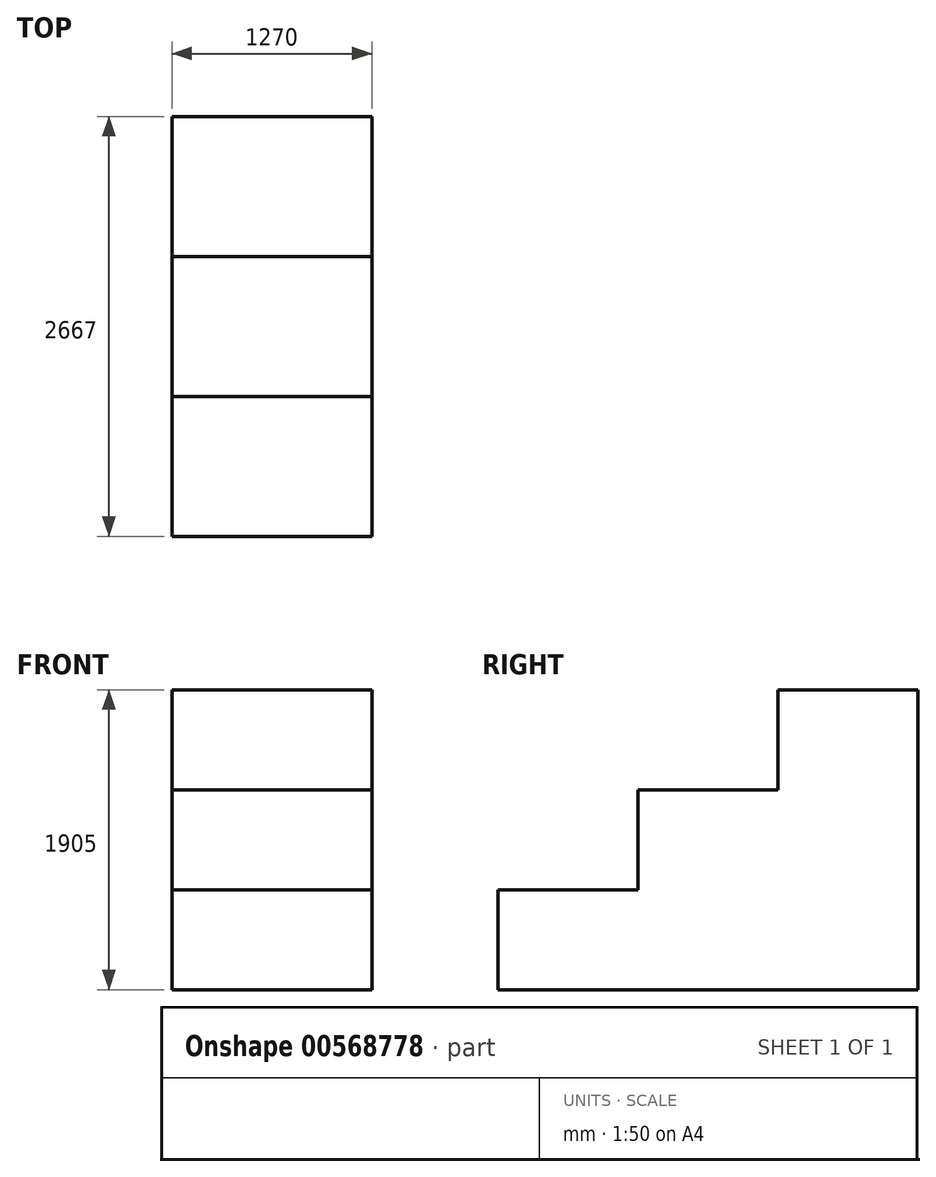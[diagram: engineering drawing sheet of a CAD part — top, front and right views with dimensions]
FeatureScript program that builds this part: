
annotation { "Feature Type Name" : "Feature", "Feature Type Description" : "" }
export const myFeature = defineFeature(function(context is Context, id is Id, definition is map)
    precondition{}
    {
        {
            var Q0;
            Q0=qCreatedBy(makeId("Front.planeOp"),FACE);
            var sketch = newSketch(context, id + "F0", { "sketchPlane" : qUnion([Q0])});
            skLineSegment(sketch, "E0.bottom", {"start": v(0, 0) * mm, "end": v(1270, 0) * mm});
            skLineSegment(sketch, "E0.top", {"start": v(0, -635) * mm, "end": v(1270, -635) * mm});
            skLineSegment(sketch, "E0.left", {"start": v(0, 0) * mm, "end": v(0, -635) * mm});
            skLineSegment(sketch, "E0.right", {"start": v(1270, 0) * mm, "end": v(1270, -635) * mm});
            skSolve(sketch);
        }
        {
            var Q0;
            Q0=makeQuery(id+"F0.imprint","IMPRINT",FACE,{"disambiguationData":[TD([[makeQuery(id+"F0.imprint","IMPRINT",EDGE,{"derivedFrom":sQuery(id+"F0.wireOp",EDGE,"E0.bottom")}),-1.0]])]});
            extrude(context, id + "F1", {"entities" : qUnion([Q0]), "depth" : 2667 * mm, "offsetDistance" : 25.4 * mm});
        }
        {
            var Q0;
            Q0=makeQuery(id+"F1.opExtrude","SWEPT_FACE",FACE,{"disambiguationData":[OSD([sQuery(id+"F0.wireOp",EDGE,"E0.right")])]});
            var sketch = newSketch(context, id + "F2", { "sketchPlane" : qUnion([Q0])});
            skLineSegment(sketch, "E1.bottom", {"start": v(0, 0) * mm, "end": v(-889, 0) * mm});
            skLineSegment(sketch, "E1.top", {"start": v(0, 1270) * mm, "end": v(-889, 1270) * mm});
            skLineSegment(sketch, "E1.left", {"start": v(0, 0) * mm, "end": v(0, 1270) * mm});
            skLineSegment(sketch, "E1.right", {"start": v(-889, 0) * mm, "end": v(-889, 1270) * mm});
            skSolve(sketch);
        }
        {
            var Q0;
            Q0=makeQuery(id+"F2.imprint","IMPRINT",FACE,{"disambiguationData":[TD([[makeQuery(id+"F2.imprint","IMPRINT",EDGE,{"derivedFrom":sQuery(id+"F2.wireOp",EDGE,"E1.bottom")}),1.0]])]});
            extrude(context, id + "F3", {"entities" : qUnion([Q0]), "operationType" : NewBodyOperationType.ADD, "oppositeDirection" : true, "depth" : 1270 * mm, "offsetDistance" : 25.4 * mm});
        }
        {
            var Q0;
            Q0=makeQuery(id+"F3.boolean.opBoolean","MERGE",FACE,{"derivedFrom":[makeQuery(id+"F1.opExtrude","SWEPT_FACE",FACE,{"disambiguationData":[OSD([sQuery(id+"F0.wireOp",EDGE,"E0.right")])]}),makeQuery(id+"F3.opExtrude","CAP_FACE",FACE,{"disambiguationData":[OSD([sQuery(id+"F2.wireOp",EDGE,"E1.bottom"),sQuery(id+"F2.wireOp",EDGE,"E1.top"),sQuery(id+"F2.wireOp",EDGE,"E1.left"),sQuery(id+"F2.wireOp",EDGE,"E1.right")])],"isStart":true})]});
            var sketch = newSketch(context, id + "F4", { "sketchPlane" : qUnion([Q0])});
            skLineSegment(sketch, "E2.bottom", {"start": v(-889, 0) * mm, "end": v(-1778, 0) * mm});
            skLineSegment(sketch, "E2.top", {"start": v(-889, 635) * mm, "end": v(-1778, 635) * mm});
            skLineSegment(sketch, "E2.left", {"start": v(-889, 0) * mm, "end": v(-889, 635) * mm});
            skLineSegment(sketch, "E2.right", {"start": v(-1778, 0) * mm, "end": v(-1778, 635) * mm});
            skSolve(sketch);
        }
        {
            var Q0;
            Q0=makeQuery(id+"F4.imprint","IMPRINT",FACE,{"disambiguationData":[TD([[makeQuery(id+"F4.imprint","IMPRINT",EDGE,{"derivedFrom":sQuery(id+"F4.wireOp",EDGE,"E2.bottom")}),1.0]])]});
            extrude(context, id + "F5", {"entities" : qUnion([Q0]), "operationType" : NewBodyOperationType.ADD, "oppositeDirection" : true, "depth" : 1270 * mm, "offsetDistance" : 25.4 * mm});
        }
    });
